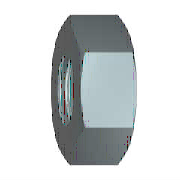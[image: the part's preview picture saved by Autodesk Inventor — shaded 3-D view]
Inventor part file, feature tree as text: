
AUTODESK INVENTOR PART (.ipt)
format: ipt  version: 2024.3 (Build 283343000, 343)  size: 162,304 bytes
history: native  units: mm (DEFAULTED — no unit token found)
features: chamfer x1, hole x1, other x1, plane x1
ambient origin geometry x7: Origin, YZ Plane, XZ Plane, X Axis, Y Axis, Z Axis, Center Point
bodies: Solid1 (feature_tree), Body (feature_tree)
feature tree (4):
  chamfer  "Chamfer1"  Distance=19.629909mm
  hole  "Thread"  [1 undecoded]
  other  "Work Axis1"
  plane  "Work Plane1"
note: 1 required parameter value undecoded (feature->parameter linkage not recoverable at this tier; creation-order binding heuristic only, values carry confidence <= 0.55)
